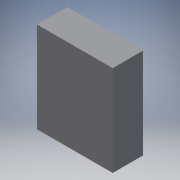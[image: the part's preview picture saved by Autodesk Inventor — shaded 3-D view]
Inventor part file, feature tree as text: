
AUTODESK INVENTOR PART (.ipt)
format: ipt  version: 2018.3 (Build 223284000, 284)  size: 193,536 bytes
history: native  units: mm
features: extrude x1, sketch x1
ambient origin geometry x8: Origin, YZ Plane, XZ Plane, XY Plane, X Axis, Y Axis, Z Axis, Center Point
bodies: Solid1 (feature_tree)
feature tree (2):
  extrude  "Extrusion1"  Depth=2.0mm
  sketch  "Sketch1"  dims[d0=5.0mm d1=2.0mm d2=6.0mm d3=0.0mm]
